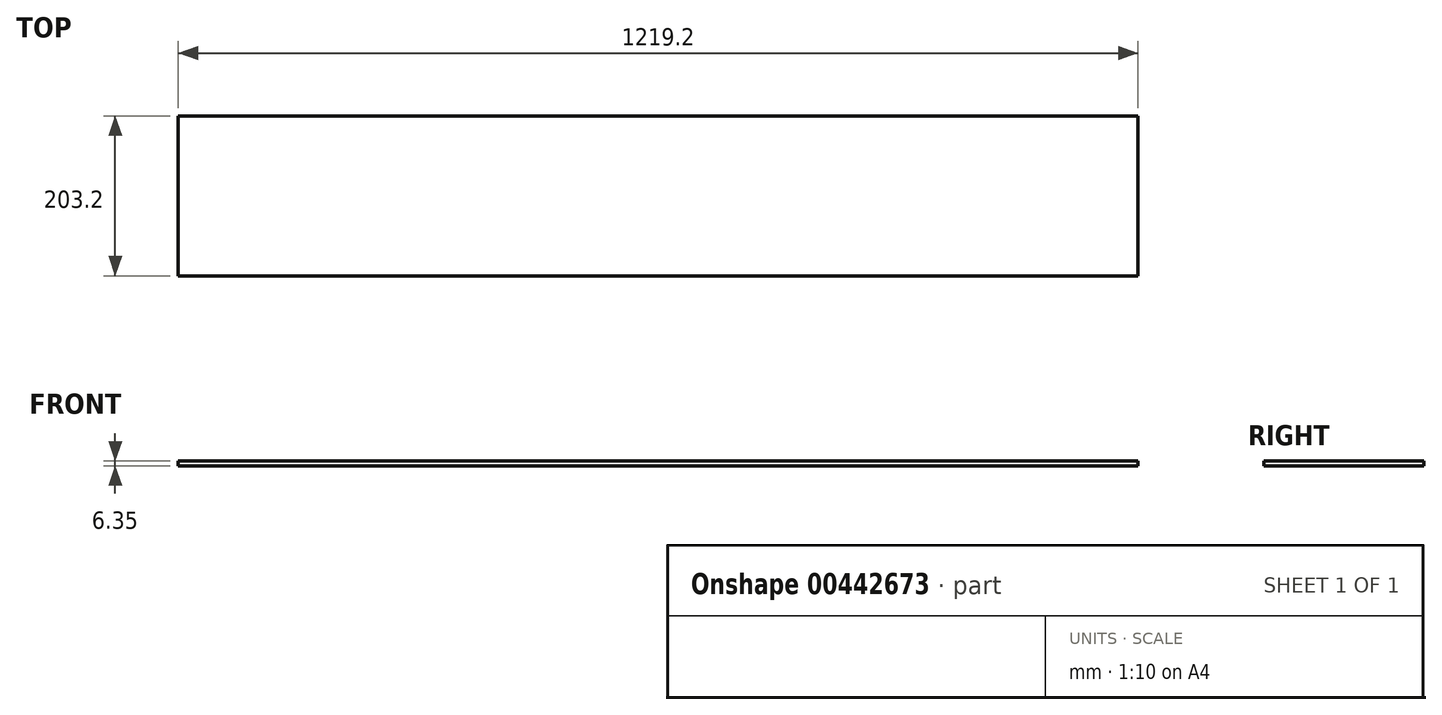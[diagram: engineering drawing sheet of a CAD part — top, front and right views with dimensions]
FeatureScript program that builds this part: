
annotation { "Feature Type Name" : "Feature", "Feature Type Description" : "" }
export const myFeature = defineFeature(function(context is Context, id is Id, definition is map)
    precondition{}
    {
        {
            var Q0;
            Q0=qCreatedBy(makeId("Top.planeOp"),FACE);
            var sketch = newSketch(context, id + "F0", { "sketchPlane" : qUnion([Q0])});
            skLineSegment(sketch, "E0.bottom", {"start": v(0, 0) * mm, "end": v(1219.2, 0) * mm});
            skLineSegment(sketch, "E0.top", {"start": v(0, 203.2) * mm, "end": v(1219.2, 203.2) * mm});
            skLineSegment(sketch, "E0.left", {"start": v(0, 0) * mm, "end": v(0, 203.2) * mm});
            skLineSegment(sketch, "E0.right", {"start": v(1219.2, 0) * mm, "end": v(1219.2, 203.2) * mm});
            skSolve(sketch);
        }
        {
            var Q0;
            Q0 = qSketchRegion(id + "F0", true);
            extrude(context, id + "F1", {"entities" : qUnion([Q0]), "depth" : 6.35 * mm});
        }
    });
